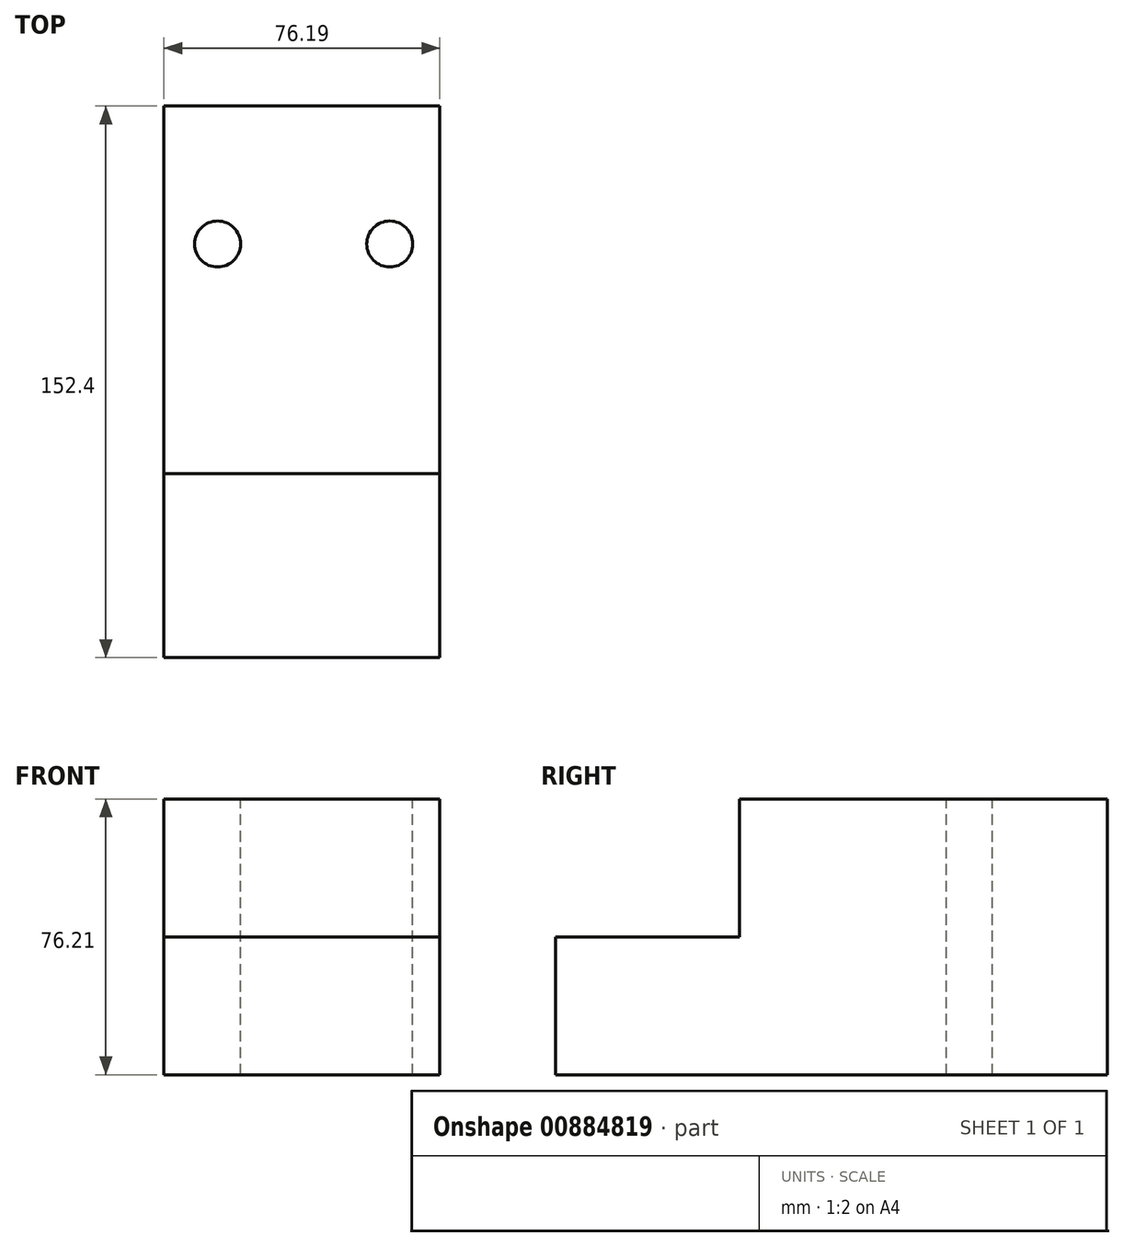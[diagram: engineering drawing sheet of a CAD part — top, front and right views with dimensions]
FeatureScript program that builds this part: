
annotation { "Feature Type Name" : "Feature", "Feature Type Description" : "" }
export const myFeature = defineFeature(function(context is Context, id is Id, definition is map)
    precondition{}
    {
        {
            var Q0;
            Q0=qCreatedBy(makeId("Front.planeOp"),FACE);
            var sketch = newSketch(context, id + "F0", { "sketchPlane" : qUnion([Q0])});
            skLineSegment(sketch, "E0", {"start": v(-45.25, 39.67) * mm, "end": v(30.94, 39.67) * mm});
            skLineSegment(sketch, "E1", {"start": v(30.94, 39.67) * mm, "end": v(30.94, -36.54) * mm});
            skLineSegment(sketch, "E2", {"start": v(-45.25, -36.54) * mm, "end": v(30.94, -36.54) * mm});
            skLineSegment(sketch, "E3", {"start": v(-45.25, -36.54) * mm, "end": v(-45.25, 39.67) * mm});
            skSolve(sketch);
        }
        {
            var Q0;
            Q0 = qSketchRegion(id + "F0", true);
            extrude(context, id + "F1", {"entities" : qUnion([Q0]), "depth" : 152.4 * mm, "offsetDistance" : 25.4 * mm});
        }
        {
            var Q0;
            Q0=makeQuery(id+"F1.opExtrude","SWEPT_FACE",FACE,{"disambiguationData":[OSD([sQuery(id+"F0.wireOp",EDGE,"E1")])]});
            var sketch = newSketch(context, id + "F2", { "sketchPlane" : qUnion([Q0])});
            skLineSegment(sketch, "E4", {"start": v(-152.4, 39.67) * mm, "end": v(-152.4, 1.57) * mm});
            skLineSegment(sketch, "E5", {"start": v(-152.4, 1.57) * mm, "end": v(-101.59, 1.57) * mm});
            skLineSegment(sketch, "E6", {"start": v(-101.59, 1.57) * mm, "end": v(-101.59, 39.67) * mm});
            skLineSegment(sketch, "E7", {"start": v(-101.59, 39.67) * mm, "end": v(-152.4, 39.67) * mm});
            skSolve(sketch);
        }
        {
            var Q0;
            Q0 = qSketchRegion(id + "F2", true);
            extrude(context, id + "F3", {"entities" : qUnion([Q0]), "operationType" : NewBodyOperationType.REMOVE, "oppositeDirection" : true, "depth" : 76.2 * mm, "offsetDistance" : 25.4 * mm});
        }
        {
            var Q0;
            Q0=makeQuery(id+"F1.opExtrude","SWEPT_FACE",FACE,{"disambiguationData":[OSD([sQuery(id+"F0.wireOp",EDGE,"E0")])]});
            var sketch = newSketch(context, id + "F4", { "sketchPlane" : qUnion([Q0])});
            skCircle(sketch, "E8", {"center": v(-30.43, -38.1) * mm, "radius": 6.35 * mm});
            skCircle(sketch, "E9", {"center": v(17.12, -38.1) * mm, "radius": 6.35 * mm});
            skSolve(sketch);
        }
        {
            var Q0;
            Q0 = qSketchRegion(id + "F4", true);
            extrude(context, id + "F5", {"entities" : qUnion([Q0]), "operationType" : NewBodyOperationType.REMOVE, "oppositeDirection" : true, "depth" : 101.6 * mm, "offsetDistance" : 25.4 * mm});
        }
    });
